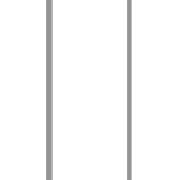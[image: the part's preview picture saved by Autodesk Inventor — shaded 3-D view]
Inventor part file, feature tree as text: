
AUTODESK INVENTOR PART (.ipt)
format: ipt  version: 2021 (Build 250183000, 183)  size: 148,992 bytes
history: native  units: in
note: dims shown in document units (in); Inventor stores cm internally (conversion verified against a paired STEP export)
features: plane x5, sketch x5, other x4, hole x1, extrude x1, boolean_combine x1
ambient origin geometry x8: Origin, YZ Plane, XZ Plane, XY Plane, X Axis, Y Axis, Z Axis, Center Point
bodies: Solid1 (feature_tree), Body (feature_tree), Solid2 (feature_tree)
feature tree (17):
  other  "Driven Length"
  other  "Frame Generator"
  plane  "Work Plane3"
  other  "Start Plane"
  other  "End Plane"
  hole  "Hole2"  [1 undecoded]
  plane  "Work Plane7"
  plane  "Work Plane8"
  plane  "Work Plane9"
  extrude  "Extrusion3"  Depth=0.0625in
  boolean_combine  "Combine1"
  sketch  "Sketch"  dims[d17=2.0in d18=0.12in d19=0.0in d22=1.5in d23=0.4375in d24=0.75in d25=0.635in d26=0.25in d27=0.5635in d28=1.0in d29=0.8108in d32=90.0deg d21=2.0in d34=0.12in d35=0.0in d8=0.5in d9=0.0344in d10=0.5in d11=0.0344in]
  sketch  "Sketch5"  dims[d0=1.5in d1=1.0in]
  sketch  "Sketch8"  dims[d2=0.0625in d3=0.0625in]
  plane  "Work Plane6"
  sketch  "Sketch9"  dims[d4=2.0in]
  sketch  "Sketch10"  dims[d16=-0.0in]
note: 1 required parameter value undecoded (feature->parameter linkage not recoverable at this tier; creation-order binding heuristic only, values carry confidence <= 0.55)
